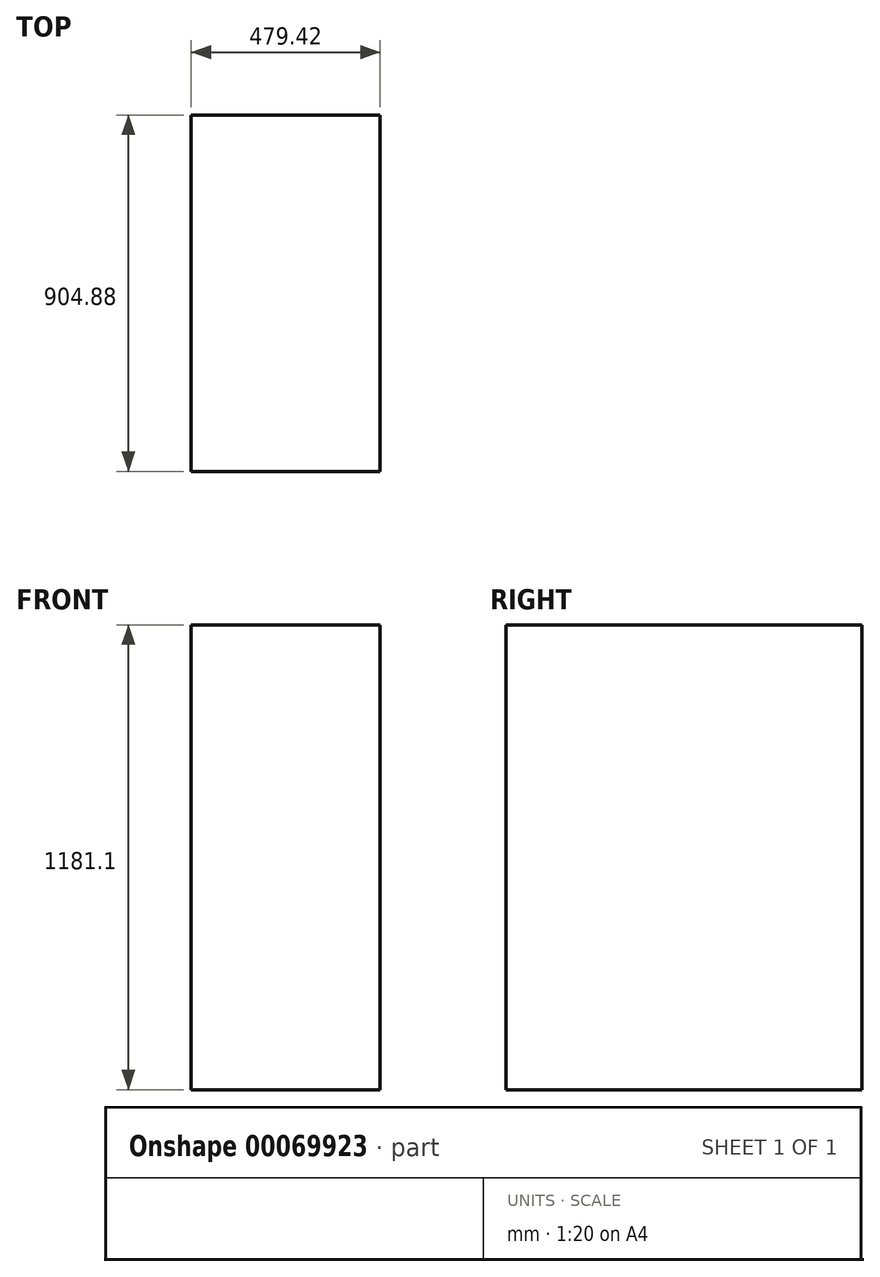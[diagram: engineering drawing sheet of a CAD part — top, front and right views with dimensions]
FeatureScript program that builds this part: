
annotation { "Feature Type Name" : "Feature", "Feature Type Description" : "" }
export const myFeature = defineFeature(function(context is Context, id is Id, definition is map)
    precondition{}
    {
        {
            var Q0;
            Q0=qCreatedBy(makeId("Top.planeOp"),FACE);
            var sketch = newSketch(context, id + "F0", { "sketchPlane" : qUnion([Q0])});
            skLineSegment(sketch, "E0.bottom", {"start": v(239.71, 452.44) * mm, "end": v(-239.71, 452.44) * mm});
            skLineSegment(sketch, "E0.top", {"start": v(239.71, -452.44) * mm, "end": v(-239.71, -452.44) * mm});
            skLineSegment(sketch, "E0.left", {"start": v(239.71, 452.44) * mm, "end": v(239.71, -452.44) * mm});
            skLineSegment(sketch, "E0.right", {"start": v(-239.71, 452.44) * mm, "end": v(-239.71, -452.44) * mm});
            skPoint(sketch, "E0.middle", {"position": v(0, 0) * mm});
            skSolve(sketch);
        }
        {
            var Q0;
            Q0=makeQuery(id+"F0.imprint","IMPRINT",FACE,{"disambiguationData":[TD([[makeQuery(id+"F0.imprint","IMPRINT",EDGE,{"derivedFrom":sQuery(id+"F0.wireOp",EDGE,"E0.bottom")}),1.0]])]});
            extrude(context, id + "F1", {"entities" : qUnion([Q0]), "depth" : 1181.1 * mm});
        }
    });
